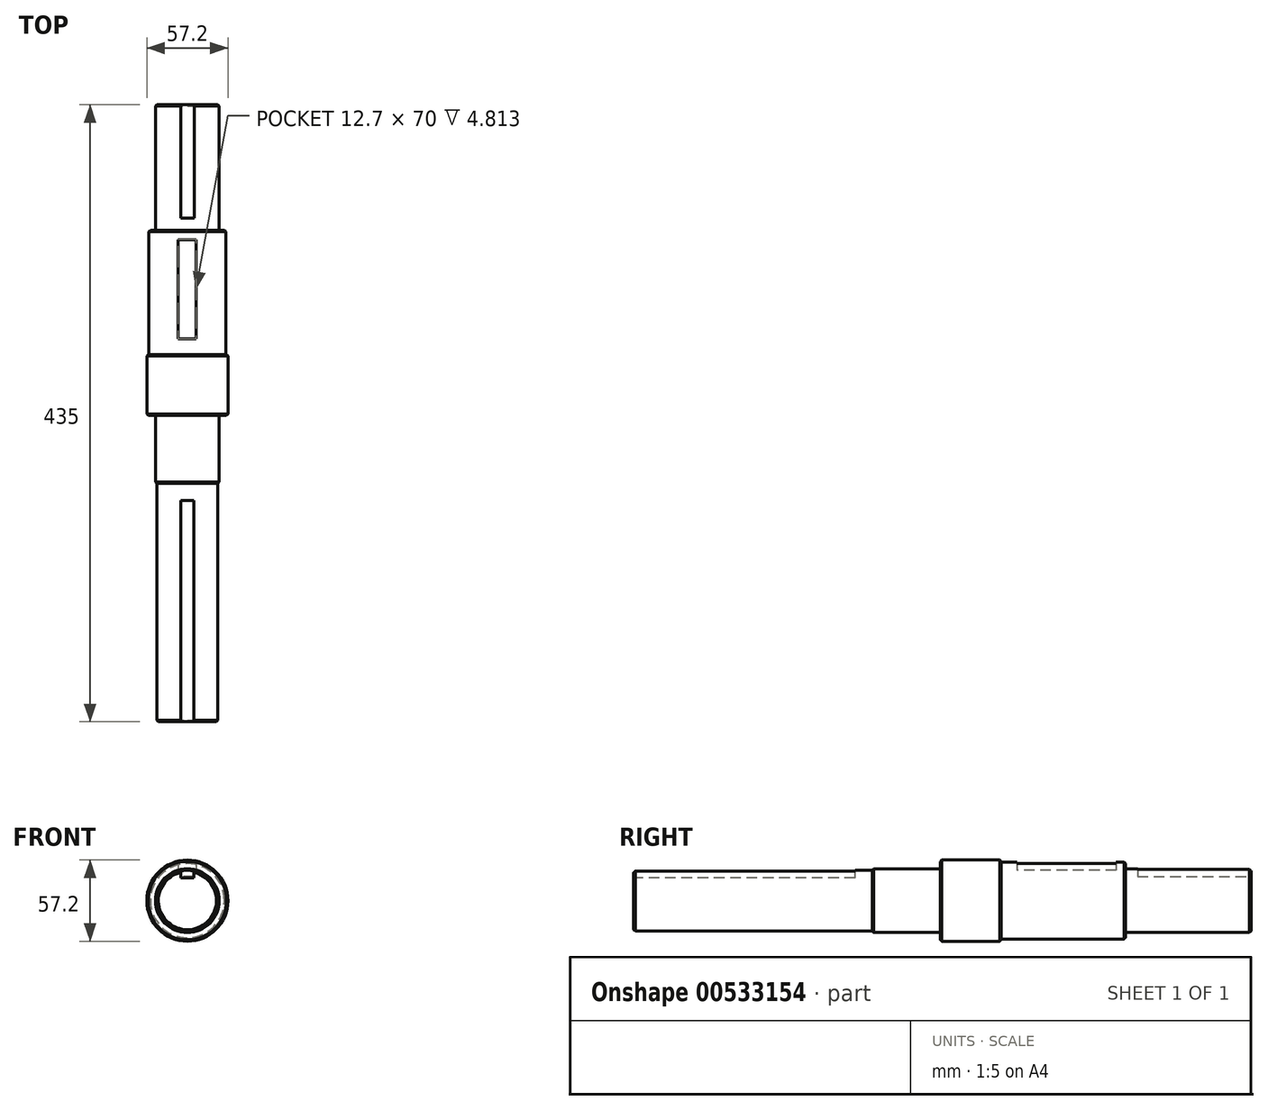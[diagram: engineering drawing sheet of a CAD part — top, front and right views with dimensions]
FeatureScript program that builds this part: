
annotation { "Feature Type Name" : "Feature", "Feature Type Description" : "" }
export const myFeature = defineFeature(function(context is Context, id is Id, definition is map)
    precondition{}
    {
        {
            var Q0;
            Q0=qCreatedBy(makeId("Right.planeOp"),FACE);
            var sketch = newSketch(context, id + "F0", { "sketchPlane" : qUnion([Q0])});
            skLineSegment(sketch, "E0.bottom", {"start": v(-216, 0) * mm, "end": v(-48, 0) * mm});
            skLineSegment(sketch, "E0.top", {"start": v(-216, 21.43) * mm, "end": v(-48, 21.43) * mm});
            skLineSegment(sketch, "E0.left", {"start": v(-216, 0) * mm, "end": v(-216, 21.43) * mm});
            skLineSegment(sketch, "E0.right", {"start": v(-48, 0) * mm, "end": v(-48, 21.43) * mm});
            skLineSegment(sketch, "E1.bottom", {"start": v(-48, 0) * mm, "end": v(0, 0) * mm});
            skLineSegment(sketch, "E1.top", {"start": v(-48, 22.5) * mm, "end": v(0, 22.5) * mm});
            skLineSegment(sketch, "E1.left", {"start": v(-48, 0) * mm, "end": v(-48, 22.5) * mm});
            skLineSegment(sketch, "E1.right", {"start": v(0, 0) * mm, "end": v(0, 22.5) * mm});
            skLineSegment(sketch, "E2.bottom", {"start": v(0, 0) * mm, "end": v(43, 0) * mm});
            skLineSegment(sketch, "E2.top", {"start": v(0, 28.6) * mm, "end": v(43, 28.6) * mm});
            skLineSegment(sketch, "E2.left", {"start": v(0, 0) * mm, "end": v(0, 28.6) * mm});
            skLineSegment(sketch, "E2.right", {"start": v(43, 0) * mm, "end": v(43, 28.6) * mm});
            skLineSegment(sketch, "E3.bottom", {"start": v(43, 0) * mm, "end": v(130.5, 0) * mm});
            skLineSegment(sketch, "E3.top", {"start": v(43, 27.05) * mm, "end": v(130.5, 27.05) * mm});
            skLineSegment(sketch, "E3.left", {"start": v(43, 0) * mm, "end": v(43, 27.05) * mm});
            skLineSegment(sketch, "E3.right", {"start": v(130.5, 0) * mm, "end": v(130.5, 27.05) * mm});
            skLineSegment(sketch, "E4.bottom", {"start": v(130.5, 0) * mm, "end": v(175, 0) * mm});
            skLineSegment(sketch, "E4.top", {"start": v(130.5, 22.5) * mm, "end": v(175, 22.5) * mm});
            skLineSegment(sketch, "E4.left", {"start": v(130.5, 0) * mm, "end": v(130.5, 22.5) * mm});
            skLineSegment(sketch, "E4.right", {"start": v(175, 0) * mm, "end": v(175, 22.5) * mm});
            skLineSegment(sketch, "E5.bottom", {"start": v(175, 0) * mm, "end": v(219, 0) * mm});
            skLineSegment(sketch, "E5.top", {"start": v(175, 22.5) * mm, "end": v(219, 22.5) * mm});
            skLineSegment(sketch, "E5.right", {"start": v(219, 0) * mm, "end": v(219, 22.5) * mm});
            skSolve(sketch);
        }
        {
            var Q0;
            {var subQ0=sQuery(id+"F0.wireOp",EDGE,"E0.bottom");Q0=makeQuery(id+"F0.imprint","IMPRINT",FACE,{"disambiguationData":[TD([[makeQuery(id+"F0.imprint","IMPRINT",EDGE,{"derivedFrom":subQ0}),1.0]])]});}
            var Q1;
            {var subQ3=sQuery(id+"F0.wireOp",EDGE,"E1.bottom");Q1=makeQuery(id+"F0.imprint","IMPRINT",FACE,{"disambiguationData":[TD([[makeQuery(id+"F0.imprint","IMPRINT",EDGE,{"derivedFrom":subQ3}),1.0]])]});}
            var Q2;
            {var subQ3=sQuery(id+"F0.wireOp",EDGE,"E2.bottom");Q2=makeQuery(id+"F0.imprint","IMPRINT",FACE,{"disambiguationData":[TD([[makeQuery(id+"F0.imprint","IMPRINT",EDGE,{"derivedFrom":subQ3}),1.0]])]});}
            var Q3;
            Q3=makeQuery(id+"F0.imprint","IMPRINT",FACE,{"disambiguationData":[TD([[makeQuery(id+"F0.imprint","IMPRINT",EDGE,{"derivedFrom":sQuery(id+"F0.wireOp",EDGE,"E3.bottom")}),1.0]])]});
            var Q4;
            Q4=makeQuery(id+"F0.imprint","IMPRINT",FACE,{"disambiguationData":[TD([[makeQuery(id+"F0.imprint","IMPRINT",EDGE,{"derivedFrom":sQuery(id+"F0.wireOp",EDGE,"E4.bottom")}),1.0]])]});
            var Q5;
            Q5=makeQuery(id+"F0.imprint","IMPRINT",FACE,{"disambiguationData":[TD([[makeQuery(id+"F0.imprint","IMPRINT",EDGE,{"derivedFrom":sQuery(id+"F0.wireOp",EDGE,"E5.bottom")}),1.0]])]});
            var Q6;
            Q6=sQuery(id+"F0.wireOp",EDGE,"E5.bottom");
            revolve(context, id + "F1", {"entities" : qUnion([Q0, Q1, Q2, Q3, Q4, Q5]), "axis" : qUnion([Q6]), "revolveType" : RevolveType.FULL});
        }
        {
            var Q0;
            Q0=makeQuery(id+"F1.opRevolve","SWEPT_FACE",FACE,{"disambiguationData":[OSD([sQuery(id+"F0.wireOp",EDGE,"E0.left")])]});
            var sketch = newSketch(context, id + "F2", { "sketchPlane" : qUnion([Q0])});
            skLineSegment(sketch, "E6.bottom", {"start": v(4.46, 16) * mm, "end": v(-4.74, 16) * mm});
            skLineSegment(sketch, "E6.top", {"start": v(4.46, 26) * mm, "end": v(-4.74, 26) * mm});
            skLineSegment(sketch, "E6.left", {"start": v(4.46, 16) * mm, "end": v(4.46, 26) * mm});
            skLineSegment(sketch, "E6.right", {"start": v(-4.74, 16) * mm, "end": v(-4.74, 26) * mm});
            skSolve(sketch);
        }
        {
            var Q0;
            {var subQ0=sQuery(id+"F2.wireOp",EDGE,"E6.bottom");Q0=makeQuery(id+"F2.imprint","IMPRINT",FACE,{"disambiguationData":[TD([[makeQuery(id+"F2.imprint","IMPRINT",EDGE,{"derivedFrom":subQ0}),-1.0]])]});}
            extrude(context, id + "F3", {"entities" : qUnion([Q0]), "operationType" : NewBodyOperationType.REMOVE, "oppositeDirection" : true, "depth" : 156 * mm, "offsetDistance" : 25 * mm});
        }
        {
            var Q0;
            Q0=makeQuery(id+"F1.opRevolve","SWEPT_FACE",FACE,{"disambiguationData":[OSD([sQuery(id+"F0.wireOp",EDGE,"E0.left")])]});
            cPlane(context, id + "F4", {"entities" : qUnion([Q0]), "cplaneType" : CPlaneType.OFFSET, "offset" : 270 * mm, "oppositeDirection" : true, "width" : 150 * mm, "height" : 150 * mm});
        }
        {
            var Q0;
            Q0=qCreatedBy(id+"F4.planeOp",FACE);
            var sketch = newSketch(context, id + "F5", { "sketchPlane" : qUnion([Q0])});
            skLineSegment(sketch, "E7.bottom", {"start": v(-6.56, 28.43) * mm, "end": v(6.14, 28.43) * mm});
            skLineSegment(sketch, "E7.top", {"start": v(-6.56, 21.43) * mm, "end": v(6.14, 21.43) * mm});
            skLineSegment(sketch, "E7.left", {"start": v(-6.56, 28.43) * mm, "end": v(-6.56, 21.43) * mm});
            skLineSegment(sketch, "E7.right", {"start": v(6.14, 28.43) * mm, "end": v(6.14, 21.43) * mm});
            skSolve(sketch);
        }
        {
            var Q0;
            Q0=makeQuery(id+"F5.imprint","IMPRINT",FACE,{"disambiguationData":[TD([[makeQuery(id+"F5.imprint","IMPRINT",EDGE,{"derivedFrom":sQuery(id+"F5.wireOp",EDGE,"E7.bottom")}),-1.0]])]});
            var Q1;
            Q1=sQuery(id+"F5.wireOp",EDGE,"E7.top");
            var Q2;
            Q2=sQuery(id+"F5.wireOp",EDGE,"E7.right");
            var Q3;
            Q3=sQuery(id+"F5.wireOp",EDGE,"E7.left");
            var Q4;
            Q4=sQuery(id+"F5.wireOp",EDGE,"E7.bottom");
            extrude(context, id + "F6", {"entities" : qUnion([Q0]), "operationType" : NewBodyOperationType.REMOVE, "surfaceEntities" : qUnion([Q1, Q2, Q3, Q4]), "oppositeDirection" : true, "depth" : 70 * mm, "offsetDistance" : 25 * mm});
        }
        {
            var Q0;
            Q0=makeQuery(id+"F1.opRevolve","SWEPT_FACE",FACE,{"disambiguationData":[OSD([sQuery(id+"F0.wireOp",EDGE,"E5.right")])]});
            var sketch = newSketch(context, id + "F7", { "sketchPlane" : qUnion([Q0])});
            skLineSegment(sketch, "E8.bottom", {"start": v(-4.76, 22.55) * mm, "end": v(4.76, 22.55) * mm});
            skLineSegment(sketch, "E8.top", {"start": v(-4.76, 17.05) * mm, "end": v(4.76, 17.05) * mm});
            skLineSegment(sketch, "E8.left", {"start": v(-4.76, 22.55) * mm, "end": v(-4.76, 17.05) * mm});
            skLineSegment(sketch, "E8.right", {"start": v(4.76, 22.55) * mm, "end": v(4.76, 17.05) * mm});
            skSolve(sketch);
        }
        {
            var Q0;
            {var subQ0=sQuery(id+"F7.wireOp",EDGE,"E8.top");Q0=makeQuery(id+"F7.imprint","IMPRINT",FACE,{"disambiguationData":[TD([[makeQuery(id+"F7.imprint","IMPRINT",EDGE,{"derivedFrom":subQ0}),1.0]])]});}
            extrude(context, id + "F8", {"entities" : qUnion([Q0]), "operationType" : NewBodyOperationType.REMOVE, "oppositeDirection" : true, "depth" : 80 * mm, "offsetDistance" : 25 * mm});
        }
        {
            var Q0;
            Q0=makeQuery(id+"F1.opRevolve","SWEPT_EDGE",EDGE,{"disambiguationData":[OSD([sQuery(id+"F0.wireOp",EDGE,"E0.top"),sQuery(id+"F0.wireOp",EDGE,"E0.left")])]});
            chamfer(context, id + "F9", {"entities" : qUnion([Q0]), "width" : 1 * mm, "tangentPropagation" : true});
        }
        {
            var Q0;
            Q0=makeQuery(id+"F1.opRevolve","SWEPT_EDGE",EDGE,{"disambiguationData":[OSD([sQuery(id+"F0.wireOp",EDGE,"E1.top"),sQuery(id+"F0.wireOp",EDGE,"E1.left")])]});
            chamfer(context, id + "F10", {"entities" : qUnion([Q0]), "width" : 1 * mm, "tangentPropagation" : true});
        }
        {
            var Q0;
            Q0=makeQuery(id+"F1.opRevolve","SWEPT_EDGE",EDGE,{"disambiguationData":[OSD([sQuery(id+"F0.wireOp",EDGE,"E2.top"),sQuery(id+"F0.wireOp",EDGE,"E2.left")])]});
            var Q1;
            Q1=makeQuery(id+"F1.opRevolve","SWEPT_EDGE",EDGE,{"disambiguationData":[OSD([sQuery(id+"F0.wireOp",EDGE,"E2.top"),sQuery(id+"F0.wireOp",EDGE,"E2.right")])]});
            chamfer(context, id + "F11", {"entities" : qUnion([Q0, Q1]), "width" : 1 * mm, "tangentPropagation" : true});
        }
        {
            var Q0;
            Q0=makeQuery(id+"F1.opRevolve","SWEPT_EDGE",EDGE,{"disambiguationData":[OSD([sQuery(id+"F0.wireOp",EDGE,"E3.top"),sQuery(id+"F0.wireOp",EDGE,"E3.right")])]});
            var Q1;
            Q1=makeQuery(id+"F1.opRevolve","SWEPT_EDGE",EDGE,{"disambiguationData":[OSD([sQuery(id+"F0.wireOp",EDGE,"E5.top"),sQuery(id+"F0.wireOp",EDGE,"E5.right")])]});
            chamfer(context, id + "F12", {"entities" : qUnion([Q0, Q1]), "width" : 1 * mm, "tangentPropagation" : true});
        }
    });
